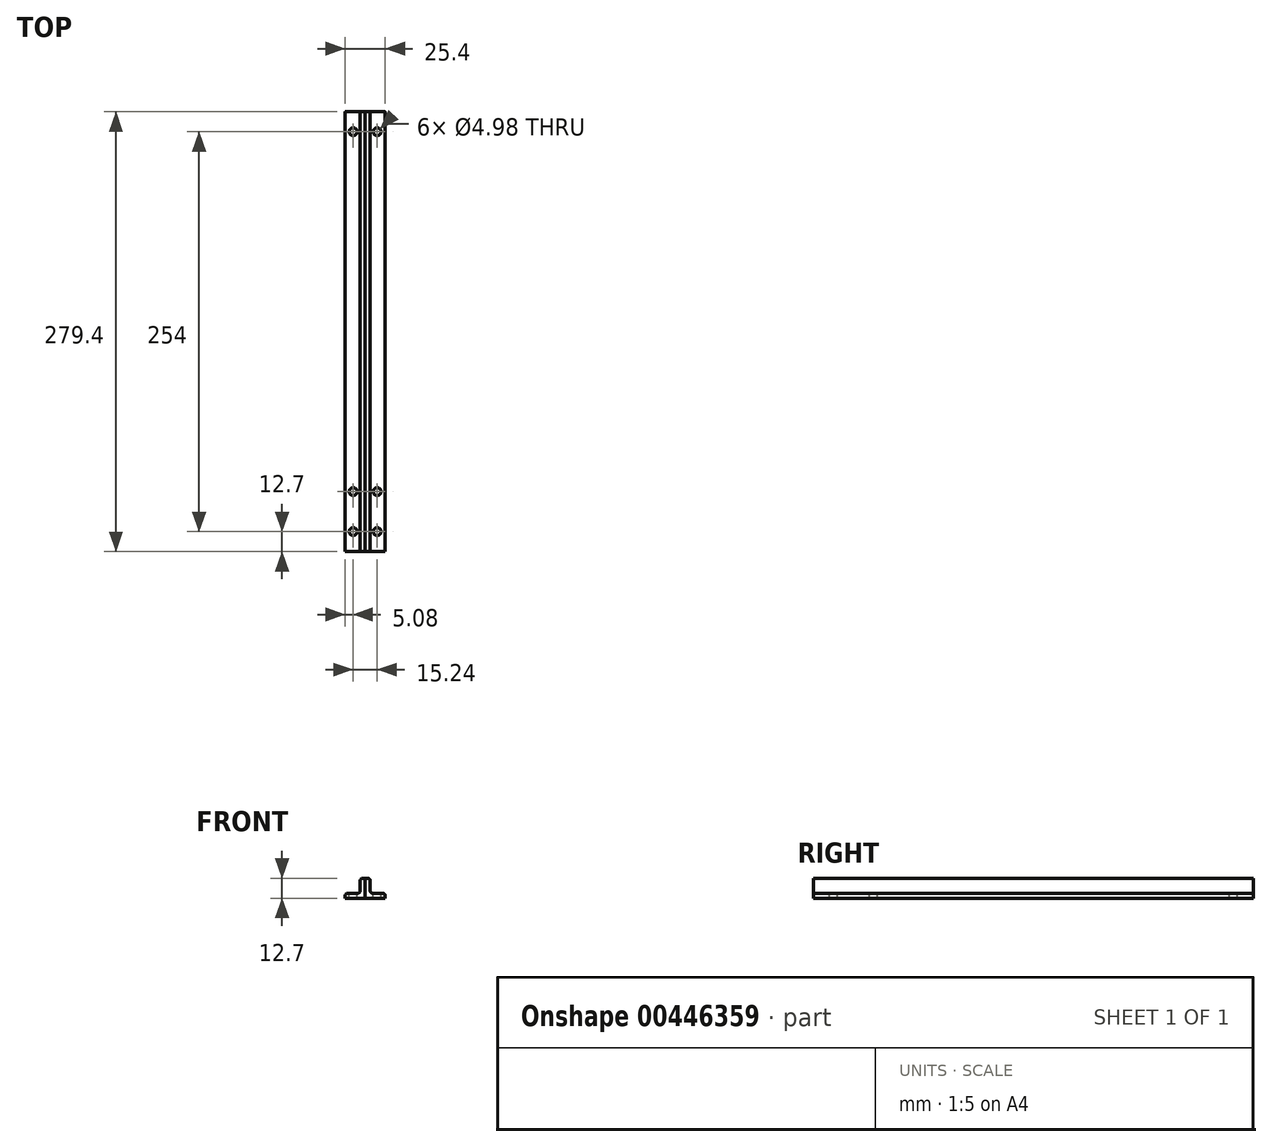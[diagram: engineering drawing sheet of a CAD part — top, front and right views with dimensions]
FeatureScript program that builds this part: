
annotation { "Feature Type Name" : "Feature", "Feature Type Description" : "" }
export const myFeature = defineFeature(function(context is Context, id is Id, definition is map)
    precondition{}
    {
        {
            var Q0;
            Q0=qCreatedBy(makeId("Front.planeOp"),FACE);
            var sketch = newSketch(context, id + "F0", { "sketchPlane" : qUnion([Q0])});
            skLineSegment(sketch, "E0", {"start": v(0, 12.7) * mm, "end": v(0, 0) * mm});
            skLineSegment(sketch, "E1", {"start": v(0, 0) * mm, "end": v(12.7, 0) * mm});
            skLineSegment(sketch, "E2", {"start": v(12.7, 0) * mm, "end": v(12.7, 0) * mm});
            skLineSegment(sketch, "E3", {"start": v(0, 12.7) * mm, "end": v(1.59, 12.7) * mm});
            skLineSegment(sketch, "E4", {"start": v(3.18, 11.11) * mm, "end": v(3.18, 4.76) * mm});
            skLineSegment(sketch, "E5", {"start": v(4.76, 3.18) * mm, "end": v(11.11, 3.18) * mm});
            skLineSegment(sketch, "E6", {"start": v(12.7, 1.59) * mm, "end": v(12.7, 0) * mm});
            skPoint(sketch, "E7.visualSharp", {"position": v(3.18, 3.17) * mm});
            skArc(sketch, "E7.filletArc", {"start": v(3.18, 4.76) * mm, "mid": v(3.64, 3.64) * mm, "end": v(4.76, 3.17) * mm});
            skPoint(sketch, "E8.visualSharp", {"position": v(3.18, 12.7) * mm});
            skArc(sketch, "E8.filletArc", {"start": v(3.18, 11.11) * mm, "mid": v(2.71, 12.24) * mm, "end": v(1.59, 12.7) * mm});
            skPoint(sketch, "E9.visualSharp", {"position": v(12.7, 3.18) * mm});
            skArc(sketch, "E9.filletArc", {"start": v(12.7, 1.59) * mm, "mid": v(12.24, 2.71) * mm, "end": v(11.11, 3.17) * mm});
            skSolve(sketch);
        }
        {
            var Q0;
            Q0=makeQuery(id+"F0.imprint","IMPRINT",FACE,{"disambiguationData":[TD([[makeQuery(id+"F0.imprint","IMPRINT",EDGE,{"derivedFrom":sQuery(id+"F0.wireOp",EDGE,"E0")}),1.0]])]});
            extrude(context, id + "F1", {"entities" : qUnion([Q0]), "depth" : 279.4 * mm, "offsetDistance" : 25.4 * mm, "symmetric" : true});
        }
        {
            var Q0;
            Q0=makeQuery(id+"F1.opExtrude","SWEPT_FACE",FACE,{"disambiguationData":[OSD([sQuery(id+"F0.wireOp",EDGE,"E1")])]});
            var sketch = newSketch(context, id + "F2", { "sketchPlane" : qUnion([Q0])});
            skPoint(sketch, "E10", {"position": v(7.62, -127) * mm});
            skPoint(sketch, "E11", {"position": v(7.62, 127) * mm});
            skPoint(sketch, "E12", {"position": v(7.62, 101.6) * mm});
            skSolve(sketch);
        }
        {
            var Q0;
            Q0=sQuery(id+"F2.wireOp",VERTEX,"E10");
            var Q1;
            Q1=sQuery(id+"F2.wireOp",VERTEX,"E12");
            var Q2;
            Q2=sQuery(id+"F2.wireOp",VERTEX,"E11");
            var Q3;
            Q3=makeQuery(id+"F1.opExtrude","SWEPT_BODY",BODY,{"disambiguationData":[OSD([sQuery(id+"F0.wireOp",EDGE,"E0"),sQuery(id+"F0.wireOp",EDGE,"E1"),sQuery(id+"F0.wireOp",EDGE,"E3"),sQuery(id+"F0.wireOp",EDGE,"E4"),sQuery(id+"F0.wireOp",EDGE,"E5"),sQuery(id+"F0.wireOp",EDGE,"E6"),sQuery(id+"F0.wireOp",EDGE,"E7.filletArc"),sQuery(id+"F0.wireOp",EDGE,"E8.filletArc"),sQuery(id+"F0.wireOp",EDGE,"E9.filletArc")])]});
            hole(context, id + "F3", {"style" : HoleStyle.SIMPLE, "endStyle" : HoleEndStyle.THROUGH, "standardTappedOrClearance" : lookupTablePath({ "standard" : "ANSI", "fit" : "Close", "size" : "#10", "type" : "Clearance" }), "standardBlindInLast" : lookupTablePath({ "fit" : "Close", "standard" : "ANSI", "size" : "#10", "type" : "Clearance" }), "holeDiameter" : 4.98 * mm, "isTappedThrough" : true, "tappedDepth" : 12.7 * mm, "tapClearance" : 3, "locations" : qUnion([Q0, Q1, Q2]), "scope" : qUnion([Q3]), "startStyle" : HoleStartStyle.PART});
        }
        {
            var Q0;
            Q0=makeQuery(id+"F1.opExtrude","SWEPT_BODY",BODY,{"disambiguationData":[OSD([sQuery(id+"F0.wireOp",EDGE,"E0"),sQuery(id+"F0.wireOp",EDGE,"E1"),sQuery(id+"F0.wireOp",EDGE,"E3"),sQuery(id+"F0.wireOp",EDGE,"E4"),sQuery(id+"F0.wireOp",EDGE,"E5"),sQuery(id+"F0.wireOp",EDGE,"E6"),sQuery(id+"F0.wireOp",EDGE,"E7.filletArc"),sQuery(id+"F0.wireOp",EDGE,"E8.filletArc"),sQuery(id+"F0.wireOp",EDGE,"E9.filletArc")])]});
            var Q1;
            Q1=qCreatedBy(makeId("Right.planeOp"),FACE);
            mirror(context, id + "F4", {"entities" : qUnion([Q0]), "mirrorPlane" : qUnion([Q1])});
        }
    });
